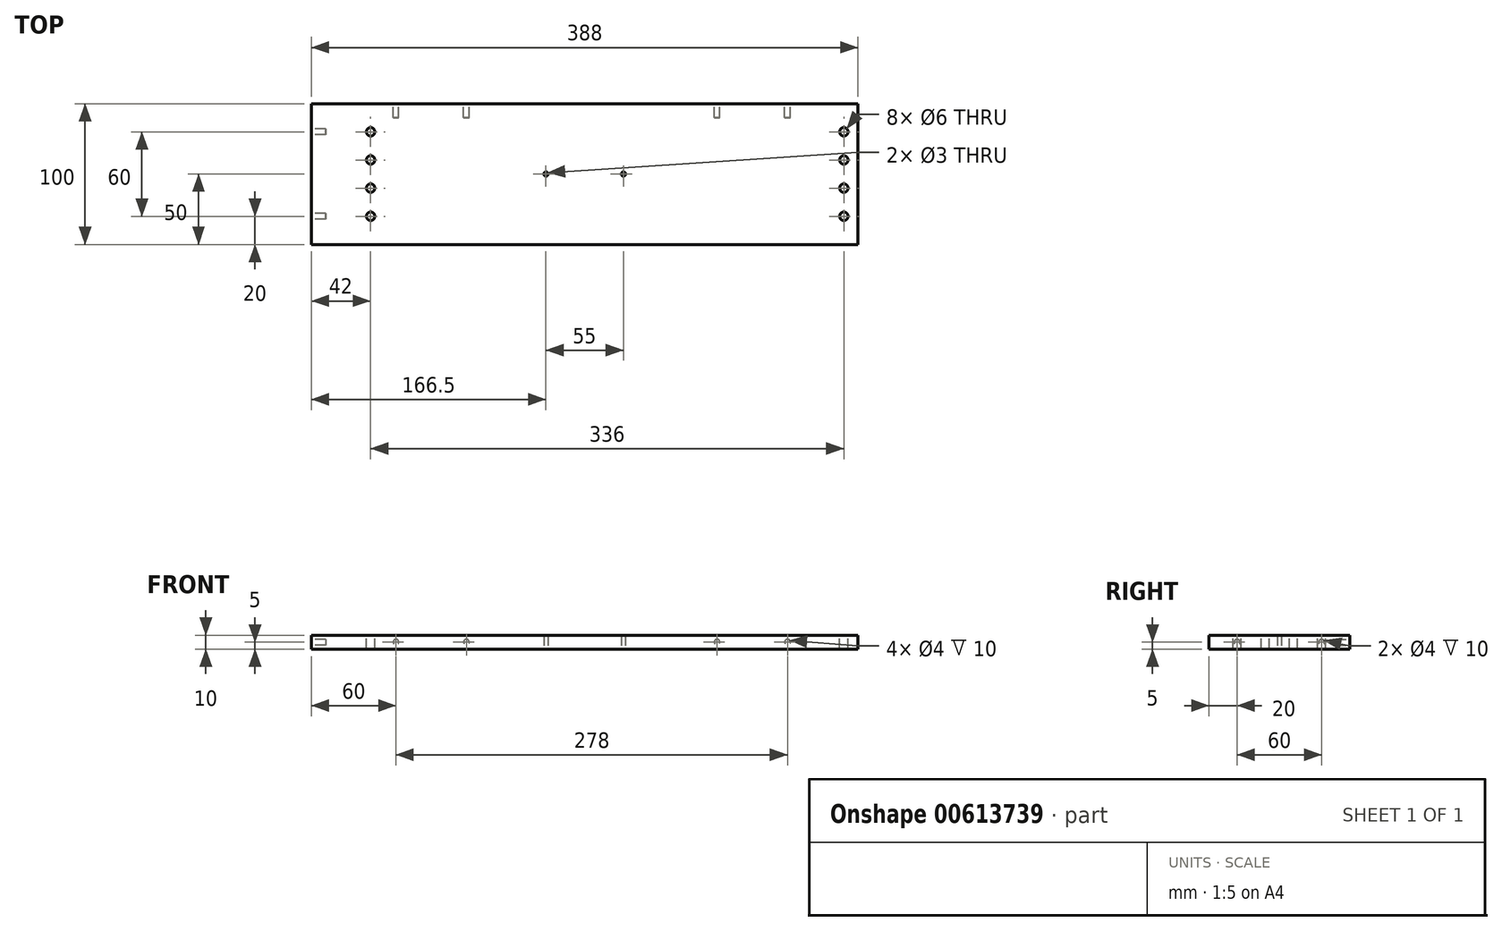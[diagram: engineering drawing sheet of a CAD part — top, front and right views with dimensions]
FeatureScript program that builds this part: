
annotation { "Feature Type Name" : "Feature", "Feature Type Description" : "" }
export const myFeature = defineFeature(function(context is Context, id is Id, definition is map)
    precondition{}
    {
        {
            var Q0;
            Q0=qCreatedBy(makeId("Top.planeOp"),FACE);
            var sketch = newSketch(context, id + "F0", { "sketchPlane" : qUnion([Q0])});
            skLineSegment(sketch, "E0.bottom", {"start": v(194, 50) * mm, "end": v(-194, 50) * mm});
            skLineSegment(sketch, "E0.top", {"start": v(194, -50) * mm, "end": v(-194, -50) * mm});
            skLineSegment(sketch, "E0.left", {"start": v(194, 50) * mm, "end": v(194, -50) * mm});
            skLineSegment(sketch, "E0.right", {"start": v(-194, 50) * mm, "end": v(-194, -50) * mm});
            skPoint(sketch, "E0.middle", {"position": v(0, 0) * mm});
            skCircle(sketch, "E1", {"center": v(-27.5, 0) * mm, "radius": 1.5 * mm});
            skCircle(sketch, "E2", {"center": v(27.5, 0) * mm, "radius": 1.5 * mm});
            skLineSegment(sketch, "E3", {"start": v(-27.5, 0) * mm, "end": v(27.5, 0) * mm, "construction": true});
            skSolve(sketch);
        }
        {
            var Q0;
            Q0=makeQuery(id+"F0.imprint","IMPRINT",FACE,{"disambiguationData":[TD([[makeQuery(id+"F0.imprint","IMPRINT",EDGE,{"derivedFrom":sQuery(id+"F0.wireOp",EDGE,"E0.bottom")}),1.0]])]});
            extrude(context, id + "F1", {"entities" : qUnion([Q0]), "depth" : 10 * mm, "offsetDistance" : 25 * mm});
        }
        {
            var Q0;
            Q0=makeQuery(id+"F1.opExtrude","SWEPT_FACE",FACE,{"disambiguationData":[OSD([sQuery(id+"F0.wireOp",EDGE,"E0.bottom")])]});
            var sketch = newSketch(context, id + "F2", { "sketchPlane" : qUnion([Q0])});
            skCircle(sketch, "E4", {"center": v(-144, 5) * mm, "radius": 2 * mm});
            skCircle(sketch, "E5", {"center": v(134, 5) * mm, "radius": 2 * mm});
            skCircle(sketch, "E6", {"center": v(-94, 5) * mm, "radius": 2 * mm});
            skCircle(sketch, "E7", {"center": v(84, 5) * mm, "radius": 2 * mm});
            skSolve(sketch);
        }
        {
            var Q0;
            Q0=qSketchRegion(id+"F2",true);
            extrude(context, id + "F3", {"entities" : qUnion([Q0]), "operationType" : NewBodyOperationType.REMOVE, "oppositeDirection" : true, "depth" : 10 * mm, "offsetDistance" : 25 * mm});
        }
        {
            var Q0;
            Q0=makeQuery(id+"F1.opExtrude","SWEPT_FACE",FACE,{"disambiguationData":[OSD([sQuery(id+"F0.wireOp",EDGE,"E0.right")])]});
            var sketch = newSketch(context, id + "F4", { "sketchPlane" : qUnion([Q0])});
            skCircle(sketch, "E8", {"center": v(-30, 5) * mm, "radius": 2 * mm});
            skCircle(sketch, "E9", {"center": v(30, 5) * mm, "radius": 2 * mm});
            skSolve(sketch);
        }
        {
            var Q0;
            Q0=qSketchRegion(id+"F4",true);
            extrude(context, id + "F5", {"entities" : qUnion([Q0]), "operationType" : NewBodyOperationType.REMOVE, "oppositeDirection" : true, "depth" : 10 * mm, "offsetDistance" : 25 * mm});
        }
        {
            var Q0;
            Q0=makeQuery(id+"F1.opExtrude","CAP_FACE",FACE,{"disambiguationData":[OSD([sQuery(id+"F0.wireOp",EDGE,"E0.bottom"),sQuery(id+"F0.wireOp",EDGE,"E0.top"),sQuery(id+"F0.wireOp",EDGE,"E0.left"),sQuery(id+"F0.wireOp",EDGE,"E0.right"),sQuery(id+"F0.wireOp",EDGE,"E1"),sQuery(id+"F0.wireOp",EDGE,"E2")])],"isStart":false});
            var sketch = newSketch(context, id + "F6", { "sketchPlane" : qUnion([Q0])});
            skCircle(sketch, "E10", {"center": v(184, -30) * mm, "radius": 3 * mm});
            skCircle(sketch, "E11", {"center": v(184, 10) * mm, "radius": 3 * mm});
            skCircle(sketch, "E12", {"center": v(184, 30) * mm, "radius": 3 * mm});
            skCircle(sketch, "E13", {"center": v(184, -10) * mm, "radius": 3 * mm});
            skLineSegment(sketch, "E14", {"start": v(184, 50) * mm, "end": v(184, 30) * mm, "construction": true});
            skLineSegment(sketch, "E15", {"start": v(184, 10) * mm, "end": v(184, 30) * mm, "construction": true});
            skLineSegment(sketch, "E16", {"start": v(184, -10) * mm, "end": v(184, 10) * mm, "construction": true});
            skLineSegment(sketch, "E17", {"start": v(184, -30) * mm, "end": v(184, -10) * mm, "construction": true});
            skLineSegment(sketch, "E18", {"start": v(184, -30) * mm, "end": v(184, -50) * mm, "construction": true});
            skLineSegment(sketch, "E19", {"start": v(-162, 50) * mm, "end": v(-162, -50) * mm, "construction": true});
            skLineSegment(sketch, "E20", {"start": v(16, 50) * mm, "end": v(16, -50) * mm, "construction": true});
            skCircle(sketch, "E21.MirrorC", {"center": v(-152, 30) * mm, "radius": 3 * mm});
            skCircle(sketch, "E22.MirrorC", {"center": v(-152, 10) * mm, "radius": 3 * mm});
            skCircle(sketch, "E23.MirrorC", {"center": v(-152, -30) * mm, "radius": 3 * mm});
            skCircle(sketch, "E24.MirrorC", {"center": v(-152, -10) * mm, "radius": 3 * mm});
            skLineSegment(sketch, "E25.MirrorCS", {"start": v(-152, -30) * mm, "end": v(-152, -10) * mm, "construction": true});
            skLineSegment(sketch, "E26.MirrorCS", {"start": v(-152, -10) * mm, "end": v(-152, 10) * mm, "construction": true});
            skLineSegment(sketch, "E27.MirrorCS", {"start": v(-152, 10) * mm, "end": v(-152, 30) * mm, "construction": true});
            skLineSegment(sketch, "E28.MirrorCS", {"start": v(-152, 50) * mm, "end": v(-152, 30) * mm, "construction": true});
            skLineSegment(sketch, "E29.MirrorCS", {"start": v(-152, -30) * mm, "end": v(-152, -50) * mm, "construction": true});
            skSolve(sketch);
        }
        {
            var Q0;
            Q0=qSketchRegion(id+"F6",true);
            extrude(context, id + "F7", {"entities" : qUnion([Q0]), "operationType" : NewBodyOperationType.REMOVE, "oppositeDirection" : true, "depth" : 25 * mm, "offsetDistance" : 25 * mm});
        }
    });
